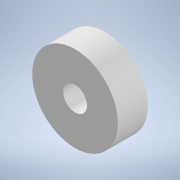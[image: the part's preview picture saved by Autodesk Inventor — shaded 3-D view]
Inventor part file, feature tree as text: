
AUTODESK INVENTOR PART (.ipt)
format: ipt  version: 2022 (Build 260153000, 153)  size: 97,792 bytes
history: native  units: mm
features: other x2, extrude x1, sketch x1, reference x1
ambient origin geometry x8: Origin, YZ Plane, XZ Plane, XY Plane, X Axis, Y Axis, Z Axis, Center Point
bodies: Solid1 (feature_tree)
feature tree (5):
  extrude  "Extrusion1"  Depth=7.5mm
  sketch  "Sketch1"  dims[d0=6.0mm d1=21.5mm d2=7.5mm d3=0.0mm]
  reference  "Reference1"
  other  "Caja_Reductora_.iam"
  other  "Base:1"
